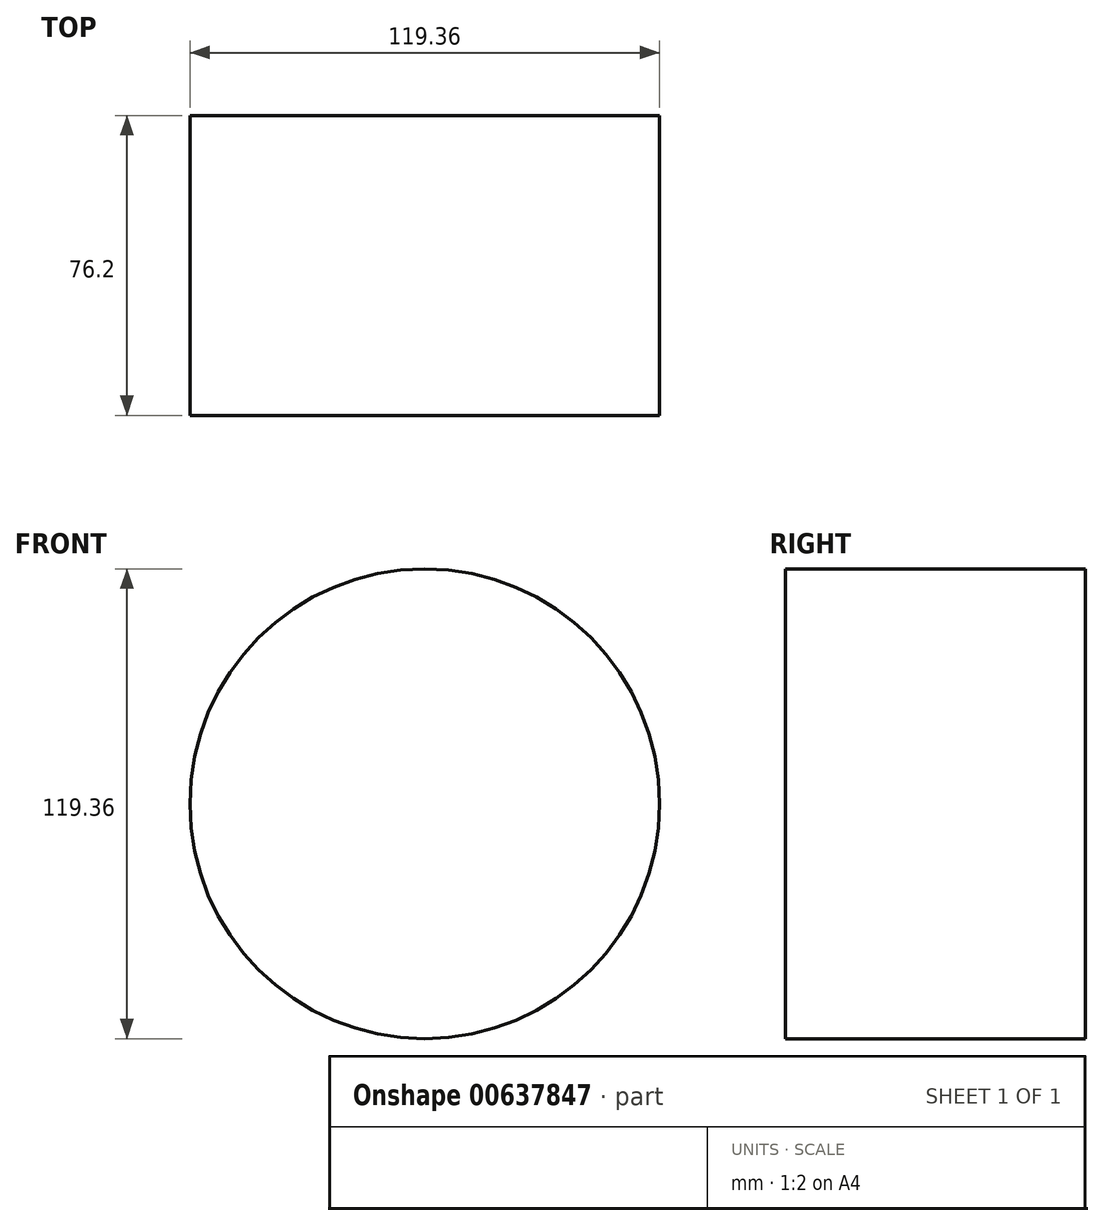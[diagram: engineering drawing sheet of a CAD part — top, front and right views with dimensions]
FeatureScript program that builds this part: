
annotation { "Feature Type Name" : "Feature", "Feature Type Description" : "" }
export const myFeature = defineFeature(function(context is Context, id is Id, definition is map)
    precondition{}
    {
        {
            var Q0;
            Q0=qCreatedBy(makeId("Front.planeOp"),FACE);
            var sketch = newSketch(context, id + "F0", { "sketchPlane" : qUnion([Q0])});
            skCircle(sketch, "E0", {"center": v(0, 0) * mm, "radius": 59.68 * mm});
            skSolve(sketch);
        }
        {
            var Q0;
            Q0=makeQuery(id+"F0.imprint","IMPRINT",FACE,{"disambiguationData":[TD([[makeQuery(id+"F0.imprint","IMPRINT",EDGE,{"derivedFrom":sQuery(id+"F0.wireOp",EDGE,"E0")}),1.0]])]});
            extrude(context, id + "F1", {"entities" : qUnion([Q0]), "depth" : 76.2 * mm, "offsetDistance" : 25.4 * mm});
        }
    });
